# Revit family: FU_Stool_Sandler_Main-1121
name_source: partatom
category: Furniture
units: mm (PartAtom-declared; Revit-internal decimal feet)

## family parameters
Always vertical = Yes
Cut with Voids When Loaded = No
OmniClass Number = 23.40.20.00
OmniClass Title = General Furniture and Specialties
Room Calculation Point = No
Shared = No
Work Plane-Based = No

## types (1)
- Main 1121
    AC Colors = Metal - Paint -AL VR - Curry
    Default Elevation = 0 mm  [stored 0 ft]
    Depth = 390 mm  [stored 1.27953 ft]
    Description = Low stool with swivel seat in Ash wood on a steel frame
    Height = 490 mm  [stored 1.60761 ft]
    Manufacturer = Sandler
    Model = Main 1121
    URL = https://www.sandlerseating.com
    Width = 410 mm  [stored 1.34514 ft]
    Wood Seat = Wood - Beech - Dark Brown Stained

note: [stored X ft] marks values corroborated as IEEE doubles in the binary element streams (Revit-internal decimal feet)

## geometry (parser evidence)
native form markers: Sweep x3
no freeform markers — native parametric forms only
